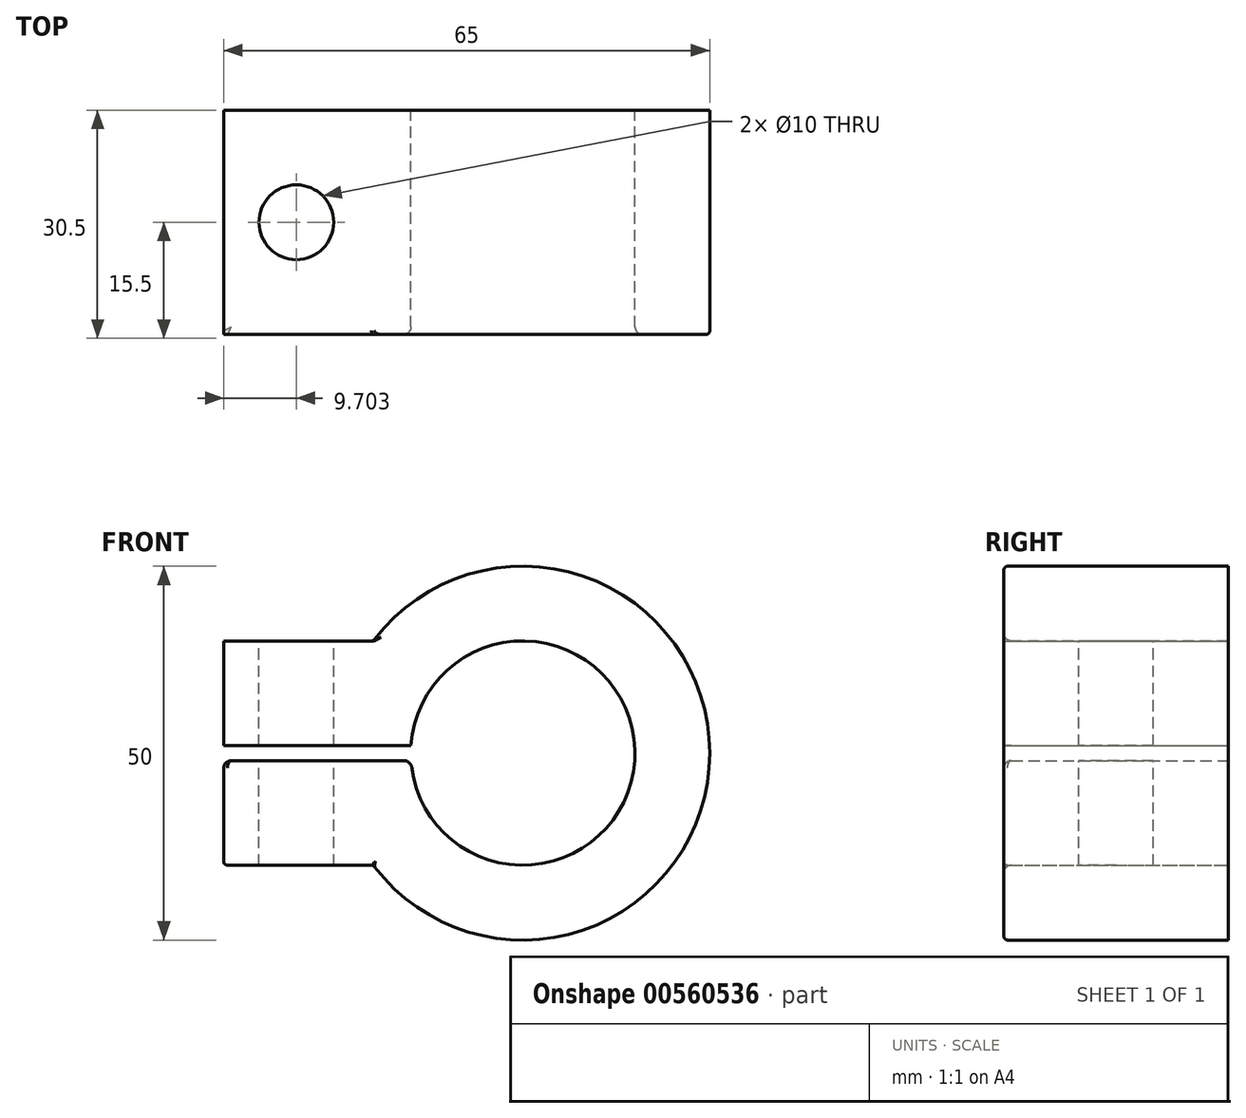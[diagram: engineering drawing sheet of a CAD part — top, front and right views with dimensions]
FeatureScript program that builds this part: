
annotation { "Feature Type Name" : "Feature", "Feature Type Description" : "" }
export const myFeature = defineFeature(function(context is Context, id is Id, definition is map)
    precondition{}
    {
        {
            var Q0;
            Q0=qCreatedBy(makeId("Front.planeOp"),FACE);
            var sketch = newSketch(context, id + "F0", { "sketchPlane" : qUnion([Q0])});
            skCircle(sketch, "E0", {"center": v(0, 0) * mm, "radius": 15 * mm});
            skCircle(sketch, "E1", {"center": v(0, 0) * mm, "radius": 25 * mm});
            skLineSegment(sketch, "E2", {"start": v(-20, 15) * mm, "end": v(-40, 15) * mm});
            skLineSegment(sketch, "E3", {"start": v(-20, -15) * mm, "end": v(-40, -15) * mm});
            skLineSegment(sketch, "E4", {"start": v(-40, 15) * mm, "end": v(-40, 1) * mm});
            skLineSegment(sketch, "E5", {"start": v(-40, 1) * mm, "end": v(-14.97, 1) * mm});
            skLineSegment(sketch, "E6", {"start": v(-40, -15) * mm, "end": v(-40, -1) * mm});
            skLineSegment(sketch, "E7", {"start": v(-40, -1) * mm, "end": v(-14.97, -1) * mm});
            skSolve(sketch);
        }
        {
            var Q0;
            {var subQ0=sQuery(id+"F0.wireOp",EDGE,"E2");Q0=makeQuery(id+"F0.imprint","IMPRINT",FACE,{"disambiguationData":[TD([[makeQuery(id+"F0.imprint","IMPRINT",EDGE,{"derivedFrom":subQ0}),1.0]])]});}
            var Q1;
            {var subQ5=sQuery(id+"F0.wireOp",EDGE,"E5");var subQ7=sQuery(id+"F0.wireOp",EDGE,"E0");var subQ9=makeQuery(id+"F0.imprint","INTERSECT",VERTEX,{"derivedFrom":[subQ7,subQ5]});Q1=makeQuery(id+"F0.imprint","IMPRINT",FACE,{"disambiguationData":[TD([[makeQuery(id+"F0.imprint","IMPRINT",EDGE,{"disambiguationData":[TD([[subQ9,1.0]])],"derivedFrom":subQ7}),-1.0]])]});}
            var Q2;
            {var subQ0=sQuery(id+"F0.wireOp",EDGE,"E3");Q2=makeQuery(id+"F0.imprint","IMPRINT",FACE,{"disambiguationData":[TD([[makeQuery(id+"F0.imprint","IMPRINT",EDGE,{"derivedFrom":subQ0}),-1.0]])]});}
            extrude(context, id + "F1", {"entities" : qUnion([Q0, Q1, Q2]), "depth" : 30 * mm, "offsetDistance" : 25 * mm});
        }
        {
            var Q0;
            Q0=makeQuery(id+"F1.opExtrude","SWEPT_FACE",FACE,{"disambiguationData":[OSD([sQuery(id+"F0.wireOp",EDGE,"E2")])]});
            var sketch = newSketch(context, id + "F2", { "sketchPlane" : qUnion([Q0])});
            skCircle(sketch, "E8", {"center": v(-30.3, -15) * mm, "radius": 5 * mm});
            skPoint(sketch, "E8.centerSnap0", {"position": v(-40, -15) * mm});
            skSolve(sketch);
        }
        {
            var Q0;
            Q0=makeQuery(id+"F2.imprint","IMPRINT",FACE,{"disambiguationData":[TD([[makeQuery(id+"F2.imprint","IMPRINT",EDGE,{"derivedFrom":sQuery(id+"F2.wireOp",EDGE,"E8")}),1.0]])]});
            extrude(context, id + "F3", {"entities" : qUnion([Q0]), "operationType" : NewBodyOperationType.REMOVE, "endBound" : BoundingType.THROUGH_ALL, "oppositeDirection" : true, "depth" : 25 * mm, "offsetDistance" : 25 * mm});
        }
        {
            var Q0;
            Q0=makeQuery(id+"F1.opExtrude","CAP_EDGE",EDGE,{"disambiguationData":[OSD([sQuery(id+"F0.wireOp",EDGE,"E1")])],"isStart":false});
            fillet(context, id + "F4", {"entities" : qUnion([Q0]), "radius" : 0.5 * mm, "tangentPropagation" : true, "allowEdgeOverflow" : false});
        }
        {
            var Q0;
            Q0=makeQuery(id+"F1.opExtrude","CAP_EDGE",EDGE,{"disambiguationData":[OSD([sQuery(id+"F0.wireOp",EDGE,"E3")])],"isStart":false});
            fillet(context, id + "F5", {"entities" : qUnion([Q0]), "radius" : 0.5 * mm, "tangentPropagation" : true, "allowEdgeOverflow" : false});
        }
        {
            var Q0;
            Q0=makeQuery(id+"F1.opExtrude","CAP_EDGE",EDGE,{"disambiguationData":[OSD([sQuery(id+"F0.wireOp",EDGE,"E6")])],"isStart":false});
            fillet(context, id + "F6", {"entities" : qUnion([Q0]), "radius" : 0.5 * mm, "tangentPropagation" : true, "allowEdgeOverflow" : false});
        }
        {
            var Q0;
            Q0=makeQuery(id+"F1.opExtrude","CAP_EDGE",EDGE,{"disambiguationData":[OSD([sQuery(id+"F0.wireOp",EDGE,"E7")])],"isStart":false});
            fillet(context, id + "F7", {"entities" : qUnion([Q0]), "radius" : 1 * mm, "tangentPropagation" : true, "allowEdgeOverflow" : false});
        }
        {
            var Q0;
            Q0=makeQuery(id+"F1.opExtrude","CAP_EDGE",EDGE,{"disambiguationData":[OSD([sQuery(id+"F0.wireOp",EDGE,"E0")])],"isStart":false});
            fillet(context, id + "F8", {"entities" : qUnion([Q0]), "radius" : 1 * mm, "tangentPropagation" : true, "allowEdgeOverflow" : false});
        }
        {
            var Q0;
            Q0=makeQuery(id+"F4.opFillet","BLEND_FACE",FACE,{"disambiguationData":[OSD([sQuery(id+"F0.wireOp",EDGE,"E1")])]});
            var Q1;
            Q1=makeQuery(id+"F1.opExtrude","SWEPT_EDGE",EDGE,{"disambiguationData":[OSD([sQuery(id+"F0.wireOp",EDGE,"E1"),sQuery(id+"F0.wireOp",EDGE,"E2")])]});
            fillet(context, id + "F9", {"entities" : qUnion([Q0, Q1]), "radius" : 0.5 * mm, "tangentPropagation" : true, "allowEdgeOverflow" : false});
        }
    });
